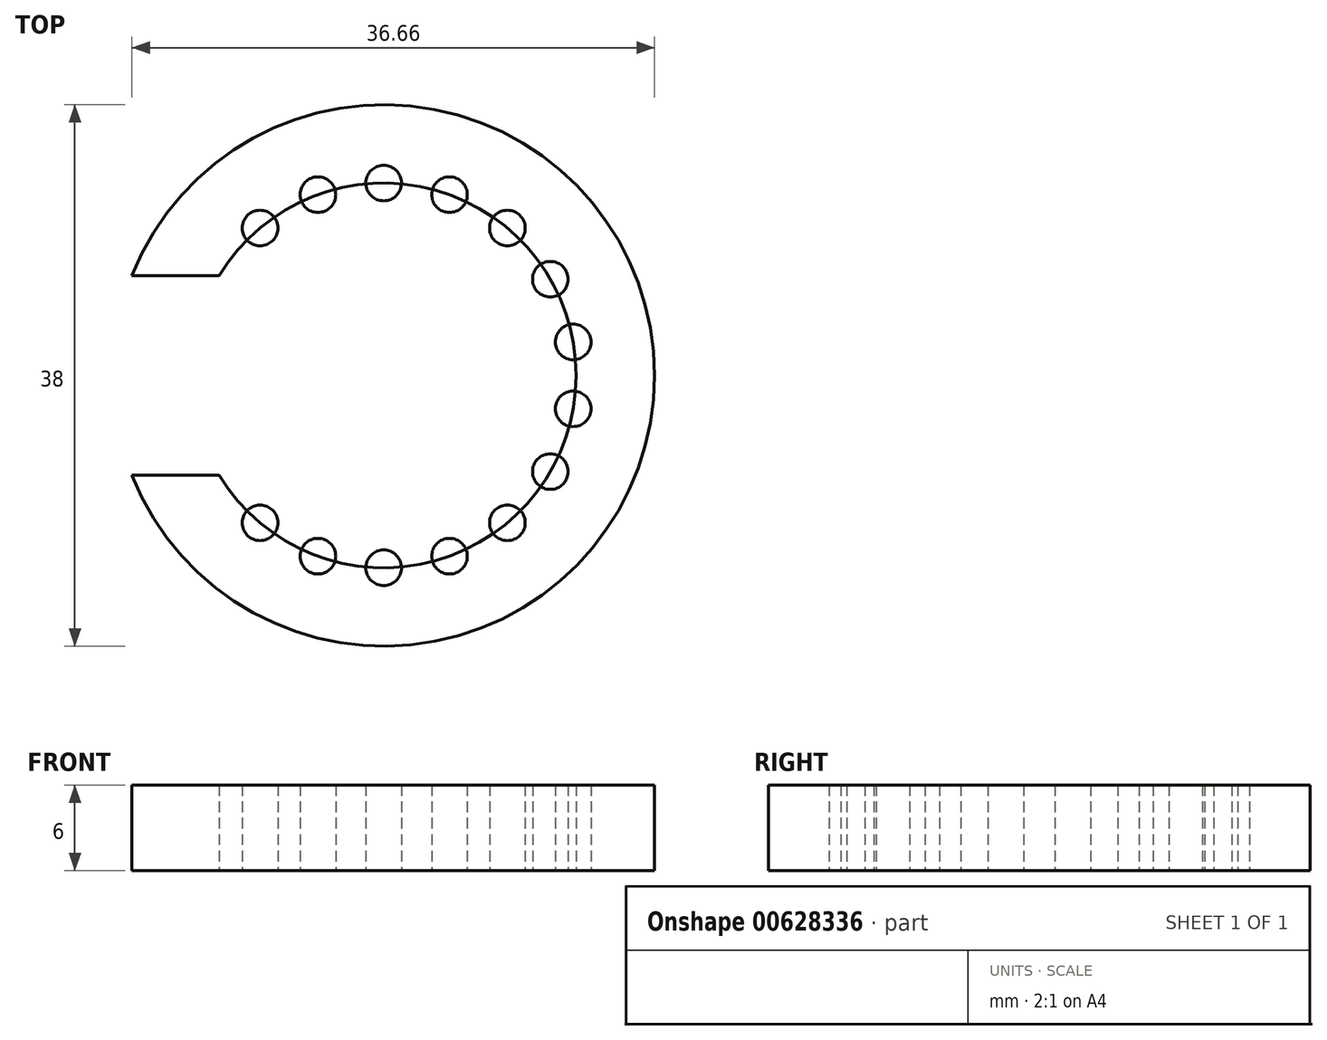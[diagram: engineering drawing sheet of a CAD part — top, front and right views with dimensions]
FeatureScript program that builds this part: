
annotation { "Feature Type Name" : "Feature", "Feature Type Description" : "" }
export const myFeature = defineFeature(function(context is Context, id is Id, definition is map)
    precondition{}
    {
        {
            var Q0;
            Q0=qCreatedBy(makeId("Top.planeOp"),FACE);
            var sketch = newSketch(context, id + "F0", { "sketchPlane" : qUnion([Q0])});
            skCircle(sketch, "E0", {"center": v(0, 0) * mm, "radius": 13.5 * mm});
            skCircle(sketch, "E1", {"center": v(0, 0) * mm, "radius": 19 * mm});
            skLineSegment(sketch, "E2", {"start": v(0, 0) * mm, "end": v(0, 7) * mm, "construction": true});
            skLineSegment(sketch, "E3", {"start": v(0, 0) * mm, "end": v(0, -7) * mm, "construction": true});
            skLineSegment(sketch, "E4", {"start": v(0, -7) * mm, "end": v(-20, -7) * mm, "construction": true});
            skLineSegment(sketch, "E5", {"start": v(0, 7) * mm, "end": v(-20, 7) * mm, "construction": true});
            skLineSegment(sketch, "E6", {"start": v(-17.66, 7) * mm, "end": v(-11.54, 7) * mm});
            skLineSegment(sketch, "E7", {"start": v(-17.66, -7) * mm, "end": v(-11.54, -7) * mm});
            skSolve(sketch);
        }
        {
            var Q0;
            {var subQ0=sQuery(id+"F0.wireOp",EDGE,"E6");Q0=makeQuery(id+"F0.imprint","IMPRINT",FACE,{"disambiguationData":[TD([[makeQuery(id+"F0.imprint","IMPRINT",EDGE,{"derivedFrom":subQ0}),1.0]])]});}
            extrude(context, id + "F1", {"entities" : qUnion([Q0]), "depth" : 6 * mm, "offsetDistance" : 25 * mm});
        }
        {
            var Q0;
            Q0=qCreatedBy(makeId("Top.planeOp"),FACE);
            var sketch = newSketch(context, id + "F2", { "sketchPlane" : qUnion([Q0])});
            skLineSegment(sketch, "E8", {"start": v(0, 0) * mm, "end": v(0, 13.5) * mm, "construction": true});
            skCircle(sketch, "E9", {"center": v(0, 13.5) * mm, "radius": 1.25 * mm});
            skSolve(sketch);
        }
        {
            var Q0;
            Q0 = qSketchRegion(id + "F2", true);
            extrude(context, id + "F3", {"entities" : qUnion([Q0]), "depth" : 6 * mm, "offsetDistance" : 25 * mm});
        }
        {
            var Q0;
            Q0=qCreatedBy(makeId("Right.planeOp"),FACE);
            var sketch = newSketch(context, id + "F4", { "sketchPlane" : qUnion([Q0])});
            skLineSegment(sketch, "E10", {"start": v(0, 0) * mm, "end": v(0, 10) * mm});
            skSolve(sketch);
        }
        {
            var Q0;
            Q0=makeQuery(id+"F3.opExtrude","SWEPT_BODY",BODY,{"disambiguationData":[OSD([sQuery(id+"F2.wireOp",EDGE,"E9")])]});
            var Q1;
            Q1=sQuery(id+"F4.wireOp",EDGE,"E10");
            circularPattern(context, id + "F5", {"entities" : qUnion([Q0]), "axis" : qUnion([Q1]), "angle" : 360 * degree, "instanceCount" : 18, "equalSpace" : true});
        }
        {
            var Q0;
            Q0=makeQuery(id+"F5.opPattern","COPY",BODY,{"derivedFrom":makeQuery(id+"F3.opExtrude","SWEPT_BODY",BODY,{"disambiguationData":[OSD([sQuery(id+"F2.wireOp",EDGE,"E9")])]}),"instanceName":"3"});
            var Q1;
            Q1=makeQuery(id+"F5.opPattern","COPY",BODY,{"derivedFrom":makeQuery(id+"F3.opExtrude","SWEPT_BODY",BODY,{"disambiguationData":[OSD([sQuery(id+"F2.wireOp",EDGE,"E9")])]}),"instanceName":"4"});
            var Q2;
            Q2=makeQuery(id+"F5.opPattern","COPY",BODY,{"derivedFrom":makeQuery(id+"F3.opExtrude","SWEPT_BODY",BODY,{"disambiguationData":[OSD([sQuery(id+"F2.wireOp",EDGE,"E9")])]}),"instanceName":"5"});
            var Q3;
            Q3=makeQuery(id+"F5.opPattern","COPY",BODY,{"derivedFrom":makeQuery(id+"F3.opExtrude","SWEPT_BODY",BODY,{"disambiguationData":[OSD([sQuery(id+"F2.wireOp",EDGE,"E9")])]}),"instanceName":"6"});
            deleteBodies(context, id + "F6", {"entities" : qUnion([Q0, Q1, Q2, Q3])});
        }
    });
